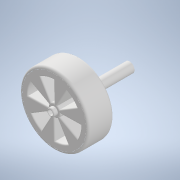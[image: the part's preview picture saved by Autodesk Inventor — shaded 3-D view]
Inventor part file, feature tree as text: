
AUTODESK INVENTOR PART (.ipt)
format: ipt  version: 2021 (Build 250183000, 183)  size: 302,080 bytes
history: native  units: mm
features: sketch x7, extrude x6, fillet x3, pattern_circular x1, hole x1
ambient origin geometry x8: Origin, YZ Plane, XZ Plane, XY Plane, X Axis, Y Axis, Z Axis, Center Point
bodies: Solid1 (feature_tree)
feature tree (18):
  extrude  "Extrusion1"  Depth=20.0mm TaperAngle=0.0deg
  fillet  "Fillet1"  Radius=2.0mm
  extrude  "Extrusion2"  Depth=10.0mm
  fillet  "Fillet2"  [1 undecoded]
  pattern_circular  "Circular Pattern1"  Count=6 Angle=360.0deg
  extrude  "Extrusion3"  Depth=3.0mm TaperAngle=0.0deg
  fillet  "Fillet3"  Radius=1.0mm
  hole  "Hole1"  [1 undecoded]
  extrude  "Extrusion4"  Depth=200.0mm TaperAngle=0.0deg
  extrude  "Extrusion5"  [1 undecoded]
  extrude  "Extrusion6"  [1 undecoded]
  sketch  "Sketch1"  dims[d0=55.0mm d1=20.0mm d2=0.0mm d3=2.0mm]
  sketch  "Sketch2"  dims[d4=42.0mm d5=10.0mm d6=30.0deg]
  sketch  "Sketch3"  dims[d7=0.0mm d8=0.0mm]
  sketch  "Sketch4"  dims[d9=1.0mm d10=60.0mm d11=360.0deg]
  sketch  "Sketch5"  dims[d13=6.0mm d14=3.0mm d15=0.0mm d16=1.0mm]
  sketch  "Sketch6"  dims[d17=4.0mm d18=6.0mm d19=4.0mm d20=2.0mm d21=90.0deg d22=8.0mm d23=20.594885mm d24=260.0mm d25=0.0mm]
  sketch  "Sketch7"  dims[d26=260.0mm d27=0.0mm d28=200.0mm d29=0.0mm]
note: 4 required parameter values undecoded (feature->parameter linkage not recoverable at this tier; creation-order binding heuristic only, values carry confidence <= 0.55)
